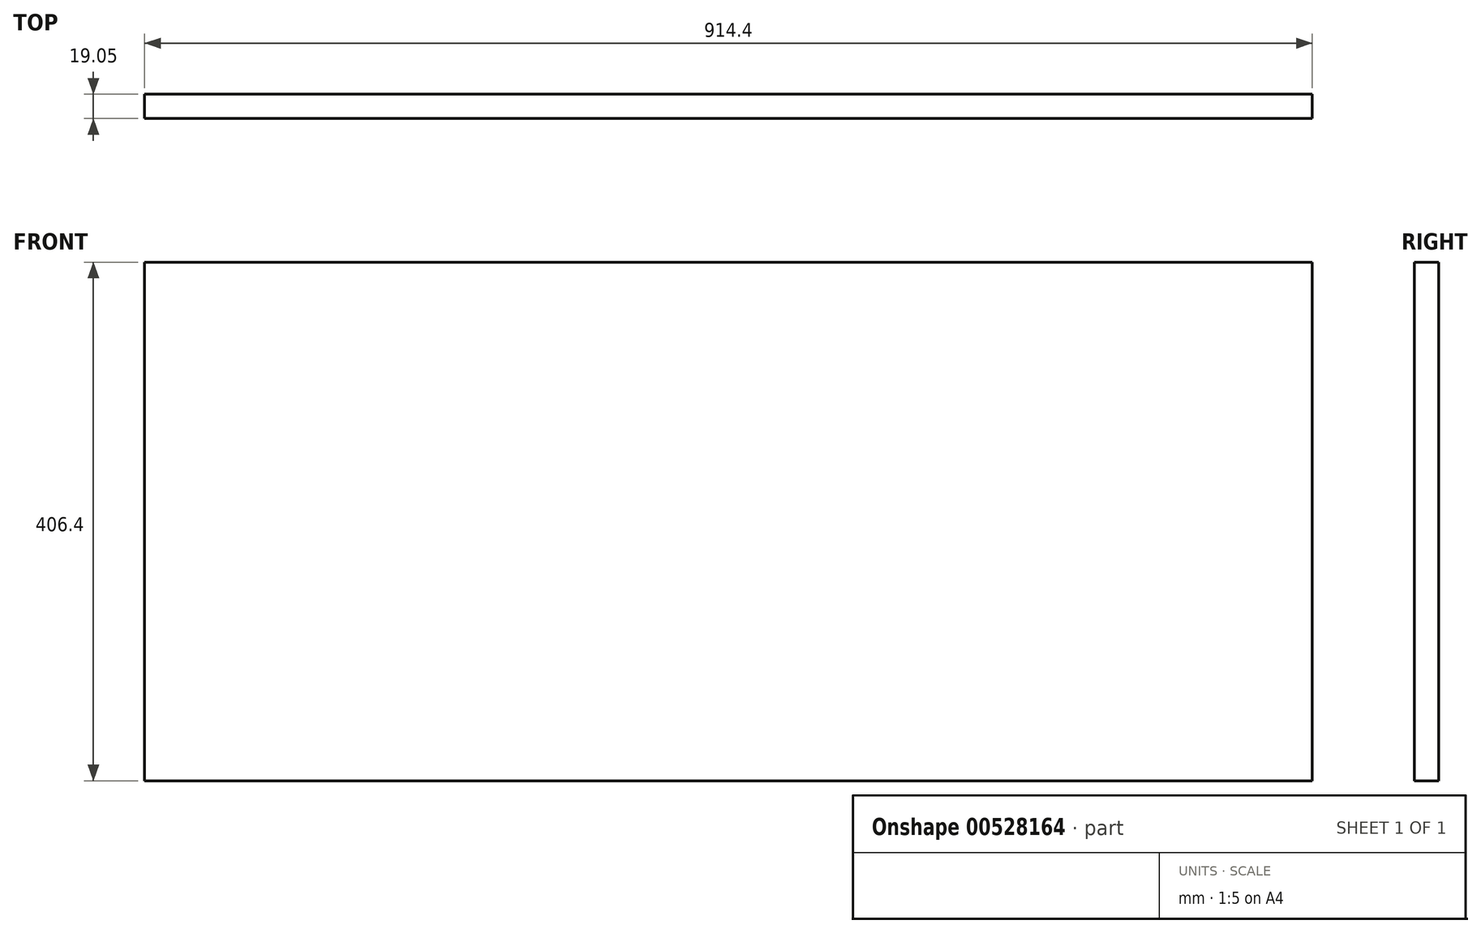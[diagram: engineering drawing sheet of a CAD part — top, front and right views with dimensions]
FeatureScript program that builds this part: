
annotation { "Feature Type Name" : "Feature", "Feature Type Description" : "" }
export const myFeature = defineFeature(function(context is Context, id is Id, definition is map)
    precondition{}
    {
        {
            var Q0;
            Q0=qCreatedBy(makeId("Front.planeOp"),FACE);
            var sketch = newSketch(context, id + "F0", { "sketchPlane" : qUnion([Q0])});
            skLineSegment(sketch, "E0.bottom", {"start": v(457.2, 203.2) * mm, "end": v(-457.2, 203.2) * mm});
            skLineSegment(sketch, "E0.top", {"start": v(457.2, -203.2) * mm, "end": v(-457.2, -203.2) * mm});
            skLineSegment(sketch, "E0.left", {"start": v(457.2, 203.2) * mm, "end": v(457.2, -203.2) * mm});
            skLineSegment(sketch, "E0.right", {"start": v(-457.2, 203.2) * mm, "end": v(-457.2, -203.2) * mm});
            skPoint(sketch, "E0.middle", {"position": v(0, 0) * mm});
            skSolve(sketch);
        }
        {
            var Q0;
            Q0=makeQuery(id+"F0.imprint","IMPRINT",FACE,{"disambiguationData":[TD([[makeQuery(id+"F0.imprint","IMPRINT",EDGE,{"derivedFrom":sQuery(id+"F0.wireOp",EDGE,"E0.bottom")}),1.0]])]});
            extrude(context, id + "F1", {"entities" : qUnion([Q0]), "depth" : 19.05 * mm, "offsetDistance" : 25.4 * mm});
        }
    });
